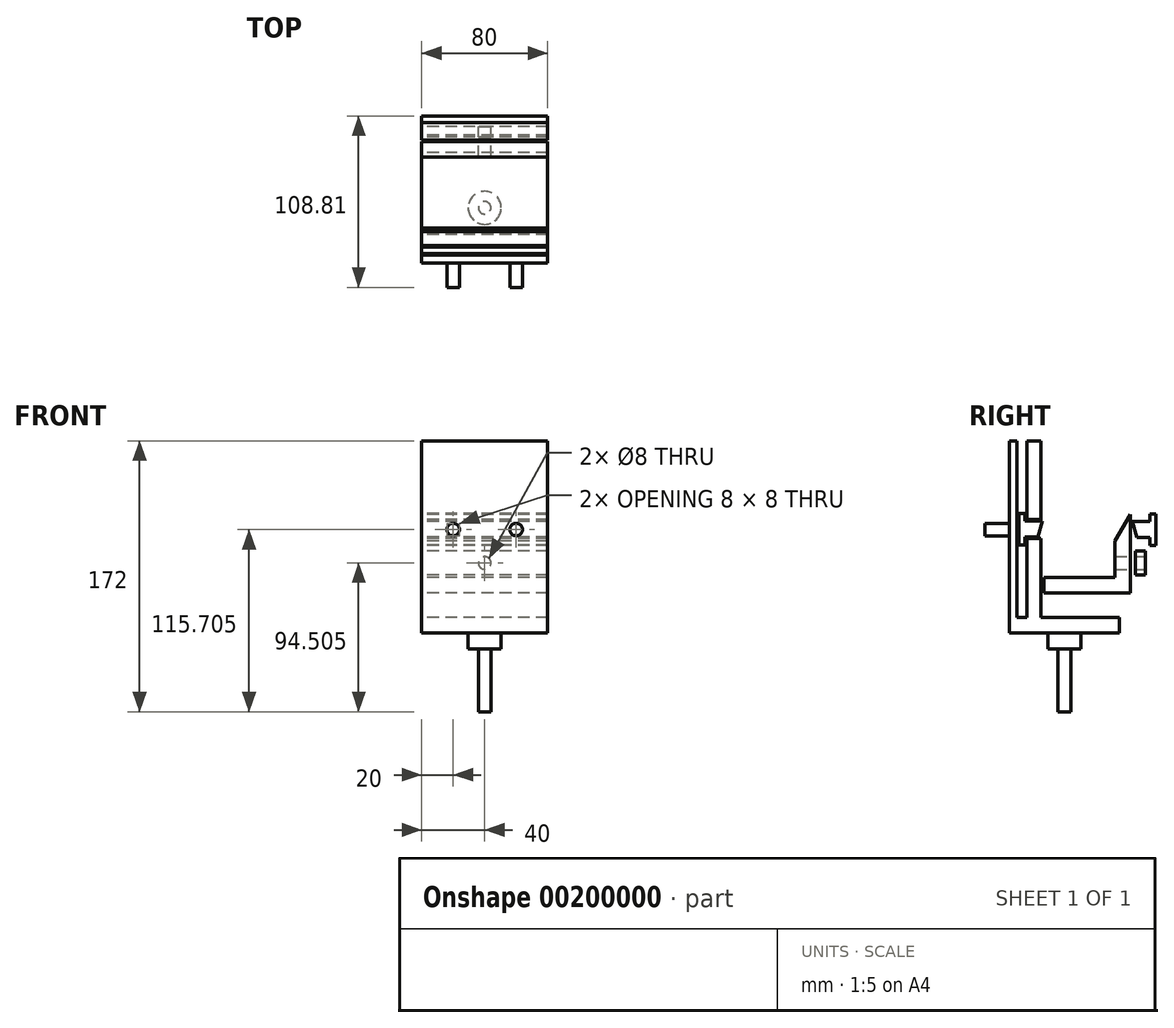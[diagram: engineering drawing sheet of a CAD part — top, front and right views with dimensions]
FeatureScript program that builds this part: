
annotation { "Feature Type Name" : "Feature", "Feature Type Description" : "" }
export const myFeature = defineFeature(function(context is Context, id is Id, definition is map)
    precondition{}
    {
        {
            var Q0;
            Q0=qCreatedBy(makeId("Right.planeOp"),FACE);
            var sketch = newSketch(context, id + "F0", { "sketchPlane" : qUnion([Q0])});
            skLineSegment(sketch, "E0", {"start": v(186.95, -108.62) * mm, "end": v(182.95, -108.62) * mm});
            skLineSegment(sketch, "E1", {"start": v(182.95, -108.62) * mm, "end": v(182.95, -113.62) * mm});
            skLineSegment(sketch, "E2", {"start": v(182.95, -113.62) * mm, "end": v(171.77, -113.62) * mm});
            skLineSegment(sketch, "E3", {"start": v(171.77, -113.62) * mm, "end": v(171.77, -123.62) * mm});
            skLineSegment(sketch, "E4", {"start": v(171.77, -123.62) * mm, "end": v(182.95, -123.62) * mm});
            skLineSegment(sketch, "E5", {"start": v(182.95, -123.62) * mm, "end": v(182.95, -128.62) * mm});
            skLineSegment(sketch, "E6", {"start": v(182.95, -128.62) * mm, "end": v(186.95, -128.62) * mm});
            skLineSegment(sketch, "E7", {"start": v(186.95, -108.62) * mm, "end": v(186.95, -128.62) * mm});
            skLineSegment(sketch, "E8.MirrorCS", {"start": v(103.77, -123.33) * mm, "end": v(103.77, -128.33) * mm});
            skLineSegment(sketch, "E9.MirrorCS", {"start": v(103.77, -108.33) * mm, "end": v(103.77, -113.33) * mm});
            skLineSegment(sketch, "E10.MirrorCS", {"start": v(103.77, -113.33) * mm, "end": v(114.77, -113.33) * mm});
            skLineSegment(sketch, "E11.MirrorCS", {"start": v(114.77, -123.33) * mm, "end": v(103.77, -123.33) * mm});
            skLineSegment(sketch, "E12.MirrorCS", {"start": v(103.77, -128.33) * mm, "end": v(99.77, -128.33) * mm});
            skLineSegment(sketch, "E13.MirrorCS", {"start": v(99.77, -108.33) * mm, "end": v(99.77, -128.33) * mm});
            skLineSegment(sketch, "E14.MirrorCS", {"start": v(99.77, -108.33) * mm, "end": v(103.77, -108.33) * mm});
            skLineSegment(sketch, "E15.MirrorCS", {"start": v(114.77, -113.33) * mm, "end": v(114.77, -123.33) * mm});
            skLineSegment(sketch, "E16.bottom", {"start": v(113.77, -112.33) * mm, "end": v(104.77, -112.33) * mm});
            skLineSegment(sketch, "E16.top", {"start": v(113.77, -62.33) * mm, "end": v(104.77, -62.33) * mm});
            skLineSegment(sketch, "E16.left", {"start": v(113.77, -112.33) * mm, "end": v(113.77, -62.33) * mm});
            skLineSegment(sketch, "E16.right", {"start": v(104.77, -112.33) * mm, "end": v(104.77, -62.33) * mm});
            skLineSegment(sketch, "E17.bottom", {"start": v(113.77, -124.33) * mm, "end": v(104.77, -124.33) * mm});
            skLineSegment(sketch, "E17.top", {"start": v(113.77, -174.33) * mm, "end": v(104.77, -174.33) * mm});
            skLineSegment(sketch, "E17.left", {"start": v(113.77, -124.33) * mm, "end": v(113.77, -174.33) * mm});
            skLineSegment(sketch, "E17.right", {"start": v(104.77, -124.33) * mm, "end": v(104.77, -174.33) * mm});
            skLineSegment(sketch, "E18.bottom", {"start": v(170.77, -109.04) * mm, "end": v(160.77, -109.04) * mm});
            skLineSegment(sketch, "E18.top", {"start": v(170.77, -159.04) * mm, "end": v(160.77, -159.04) * mm});
            skLineSegment(sketch, "E18.left", {"start": v(170.77, -109.04) * mm, "end": v(170.77, -159.04) * mm});
            skLineSegment(sketch, "E18.right", {"start": v(160.77, -109.04) * mm, "end": v(160.77, -159.04) * mm});
            skLineSegment(sketch, "E19.bottom", {"start": v(160.77, -159.04) * mm, "end": v(115.77, -159.04) * mm});
            skLineSegment(sketch, "E19.top", {"start": v(160.77, -149.04) * mm, "end": v(115.77, -149.04) * mm});
            skLineSegment(sketch, "E19.left", {"start": v(160.77, -159.04) * mm, "end": v(160.77, -149.04) * mm});
            skLineSegment(sketch, "E19.right", {"start": v(115.77, -159.04) * mm, "end": v(115.77, -149.04) * mm});
            skLineSegment(sketch, "E20.bottom", {"start": v(115.77, -149.04) * mm, "end": v(125.77, -149.04) * mm});
            skLineSegment(sketch, "E20.top", {"start": v(115.77, -109.04) * mm, "end": v(125.77, -109.04) * mm});
            skLineSegment(sketch, "E20.left", {"start": v(115.77, -149.04) * mm, "end": v(115.77, -109.04) * mm});
            skLineSegment(sketch, "E20.right", {"start": v(125.77, -149.04) * mm, "end": v(125.77, -109.04) * mm});
            skLineSegment(sketch, "E21.bottom", {"start": v(104.77, -174.33) * mm, "end": v(163.76, -174.33) * mm});
            skLineSegment(sketch, "E21.top", {"start": v(104.77, -184.33) * mm, "end": v(163.76, -184.33) * mm});
            skLineSegment(sketch, "E21.left", {"start": v(104.77, -174.33) * mm, "end": v(104.77, -184.33) * mm});
            skLineSegment(sketch, "E21.right", {"start": v(163.76, -174.33) * mm, "end": v(163.76, -184.33) * mm});
            skLineSegment(sketch, "E22.bottom", {"start": v(180.14, -132.3) * mm, "end": v(173.77, -132.3) * mm});
            skLineSegment(sketch, "E22.top", {"start": v(180.14, -147.36) * mm, "end": v(173.77, -147.36) * mm});
            skLineSegment(sketch, "E22.left", {"start": v(180.14, -132.3) * mm, "end": v(180.14, -147.36) * mm});
            skLineSegment(sketch, "E22.right", {"start": v(173.77, -132.3) * mm, "end": v(173.77, -147.36) * mm});
            skLineSegment(sketch, "E23.bottom", {"start": v(98.66, -184.33) * mm, "end": v(93.66, -184.33) * mm});
            skLineSegment(sketch, "E23.top", {"start": v(98.66, -62.33) * mm, "end": v(93.66, -62.33) * mm});
            skLineSegment(sketch, "E23.left", {"start": v(98.66, -184.33) * mm, "end": v(98.66, -62.33) * mm});
            skLineSegment(sketch, "E23.right", {"start": v(93.66, -184.33) * mm, "end": v(93.66, -62.33) * mm});
            skLineSegment(sketch, "E24.bottom", {"start": v(104.77, -174.33) * mm, "end": v(98.66, -174.33) * mm});
            skLineSegment(sketch, "E24.top", {"start": v(104.77, -184.33) * mm, "end": v(98.66, -184.33) * mm});
            skLineSegment(sketch, "E24.right", {"start": v(98.66, -174.33) * mm, "end": v(98.66, -184.33) * mm});
            skLineSegment(sketch, "E25", {"start": v(171.77, -113.62) * mm, "end": v(174.77, -123.62) * mm});
            skLineSegment(sketch, "E26", {"start": v(114.77, -113.33) * mm, "end": v(111.77, -123.33) * mm});
            skLineSegment(sketch, "E27", {"start": v(170.77, -109.04) * mm, "end": v(160.77, -126) * mm});
            skLineSegment(sketch, "E28", {"start": v(115.77, -109.04) * mm, "end": v(125.77, -123.62) * mm});
            skSolve(sketch);
        }
        {
            var Q0;
            Q0=makeQuery(id+"F0.imprint","IMPRINT",FACE,{"disambiguationData":[TD([[makeQuery(id+"F0.imprint","IMPRINT",EDGE,{"derivedFrom":sQuery(id+"F0.wireOp",EDGE,"E19.bottom")}),-1.0]])]});
            var Q1;
            Q1=makeQuery(id+"F0.imprint","IMPRINT",FACE,{"disambiguationData":[TD([[makeQuery(id+"F0.imprint","IMPRINT",EDGE,{"derivedFrom":sQuery(id+"F0.wireOp",EDGE,"E20.bottom")}),1.0]])]});
            var Q2;
            Q2=makeQuery(id+"F0.imprint","IMPRINT",FACE,{"disambiguationData":[TD([[makeQuery(id+"F0.imprint","IMPRINT",EDGE,{"derivedFrom":sQuery(id+"F0.wireOp",EDGE,"E16.bottom")}),-1.0]])]});
            var Q3;
            Q3=makeQuery(id+"F0.imprint","IMPRINT",FACE,{"disambiguationData":[TD([[makeQuery(id+"F0.imprint","IMPRINT",EDGE,{"derivedFrom":sQuery(id+"F0.wireOp",EDGE,"E8.MirrorCS")}),-1.0]])]});
            var Q4;
            Q4=makeQuery(id+"F0.imprint","IMPRINT",FACE,{"disambiguationData":[TD([[makeQuery(id+"F0.imprint","IMPRINT",EDGE,{"derivedFrom":sQuery(id+"F0.wireOp",EDGE,"E17.bottom")}),1.0]])]});
            var Q5;
            Q5=makeQuery(id+"F0.imprint","IMPRINT",FACE,{"disambiguationData":[TD([[makeQuery(id+"F0.imprint","IMPRINT",EDGE,{"derivedFrom":sQuery(id+"F0.wireOp",EDGE,"E0")}),1.0]])]});
            var Q6;
            Q6=makeQuery(id+"F0.imprint","IMPRINT",FACE,{"disambiguationData":[TD([[makeQuery(id+"F0.imprint","IMPRINT",EDGE,{"derivedFrom":sQuery(id+"F0.wireOp",EDGE,"E21.top")}),1.0]])]});
            var Q7;
            Q7=makeQuery(id+"F0.imprint","IMPRINT",FACE,{"disambiguationData":[TD([[makeQuery(id+"F0.imprint","IMPRINT",EDGE,{"derivedFrom":sQuery(id+"F0.wireOp",EDGE,"E22.bottom")}),1.0]])]});
            var Q8;
            Q8=makeQuery(id+"F0.imprint","IMPRINT",FACE,{"disambiguationData":[TD([[makeQuery(id+"F0.imprint","IMPRINT",EDGE,{"derivedFrom":sQuery(id+"F0.wireOp",EDGE,"E23.bottom")}),-1.0]])]});
            var Q9;
            Q9=makeQuery(id+"F0.imprint","IMPRINT",FACE,{"disambiguationData":[TD([[makeQuery(id+"F0.imprint","IMPRINT",EDGE,{"derivedFrom":sQuery(id+"F0.wireOp",EDGE,"E24.bottom")}),1.0]])]});
            var Q10;
            Q10=makeQuery(id+"F0.imprint","IMPRINT",FACE,{"disambiguationData":[TD([[makeQuery(id+"F0.imprint","IMPRINT",EDGE,{"derivedFrom":sQuery(id+"F0.wireOp",EDGE,"E18.top")}),-1.0]])]});
            extrude(context, id + "F1", {"entities" : qUnion([Q0, Q1, Q2, Q3, Q4, Q5, Q6, Q7, Q8, Q9, Q10]), "depth" : 80 * mm});
        }
        {
            var Q0;
            Q0=makeQuery(id+"F1.opExtrude","SWEPT_FACE",FACE,{"disambiguationData":[OSD([sQuery(id+"F0.wireOp",EDGE,"E22.left")])]});
            var sketch = newSketch(context, id + "F2", { "sketchPlane" : qUnion([Q0])});
            skCircle(sketch, "E29", {"center": v(-40, -139.82) * mm, "radius": 4 * mm});
            skPoint(sketch, "E29.centerSnap0", {"position": v(-40, -132.3) * mm});
            skPoint(sketch, "E29.centerSnap1", {"position": v(0, -139.82) * mm});
            skPoint(sketch, "E30", {"position": v(0, -118.62) * mm});
            skCircle(sketch, "E31", {"center": v(-20, -118.62) * mm, "radius": 4 * mm});
            skCircle(sketch, "E32", {"center": v(-60, -118.62) * mm, "radius": 4 * mm});
            skSolve(sketch);
        }
        {
            var Q0;
            Q0=makeQuery(id+"F2.imprint","IMPRINT",FACE,{"disambiguationData":[TD([[makeQuery(id+"F2.imprint","IMPRINT",EDGE,{"derivedFrom":sQuery(id+"F2.wireOp",EDGE,"E31")}),1.0]])]});
            var Q1;
            Q1=makeQuery(id+"F2.imprint","IMPRINT",FACE,{"disambiguationData":[TD([[makeQuery(id+"F2.imprint","IMPRINT",EDGE,{"derivedFrom":sQuery(id+"F2.wireOp",EDGE,"E32")}),1.0]])]});
            var Q2;
            Q2=makeQuery(id+"F1.opExtrude","SWEPT_BODY",BODY,{"disambiguationData":[OSD([sQuery(id+"F0.wireOp",EDGE,"E0"),sQuery(id+"F0.wireOp",EDGE,"E1"),sQuery(id+"F0.wireOp",EDGE,"E2"),sQuery(id+"F0.wireOp",EDGE,"E3"),sQuery(id+"F0.wireOp",EDGE,"E4"),sQuery(id+"F0.wireOp",EDGE,"E5"),sQuery(id+"F0.wireOp",EDGE,"E6"),sQuery(id+"F0.wireOp",EDGE,"E7")])]});
            extrude(context, id + "F3", {"entities" : qUnion([Q0, Q1]), "operationType" : NewBodyOperationType.ADD, "depth" : 1 * mm, "hasSecondDirection" : true, "secondDirectionBound" : SecondDirectionBoundingType.UP_TO_BODY, "secondDirectionOppositeDirection" : true, "secondDirectionBoundEntityBody" : qUnion([Q2]), "secondDirectionDepth" : 25 * mm});
        }
        {
            var Q0;
            Q0=makeQuery(id+"F2.imprint","IMPRINT",FACE,{"disambiguationData":[TD([[makeQuery(id+"F2.imprint","IMPRINT",EDGE,{"derivedFrom":sQuery(id+"F2.wireOp",EDGE,"E29")}),1.0]])]});
            extrude(context, id + "F4", {"entities" : qUnion([Q0]), "operationType" : NewBodyOperationType.REMOVE, "oppositeDirection" : true, "depth" : 36.3 * mm});
        }
        {
            var Q0;
            Q0=makeQuery(id+"F2.imprint","IMPRINT",FACE,{"disambiguationData":[TD([[makeQuery(id+"F2.imprint","IMPRINT",EDGE,{"derivedFrom":sQuery(id+"F2.wireOp",EDGE,"E32")}),1.0]])]});
            var Q1;
            Q1=makeQuery(id+"F2.imprint","IMPRINT",FACE,{"disambiguationData":[TD([[makeQuery(id+"F2.imprint","IMPRINT",EDGE,{"derivedFrom":sQuery(id+"F2.wireOp",EDGE,"E31")}),1.0]])]});
            var Q2;
            Q2=makeQuery(id+"F1.opExtrude","CAP_FACE",FACE,{"disambiguationData":[OSD([sQuery(id+"F0.wireOp",EDGE,"E17.bottom"),sQuery(id+"F0.wireOp",EDGE,"E17.left"),sQuery(id+"F0.wireOp",EDGE,"E17.right"),sQuery(id+"F0.wireOp",EDGE,"E21.bottom"),sQuery(id+"F0.wireOp",EDGE,"E21.top"),sQuery(id+"F0.wireOp",EDGE,"E21.right"),sQuery(id+"F0.wireOp",EDGE,"E23.bottom"),sQuery(id+"F0.wireOp",EDGE,"E23.top"),sQuery(id+"F0.wireOp",EDGE,"E23.left"),sQuery(id+"F0.wireOp",EDGE,"E23.right"),sQuery(id+"F0.wireOp",EDGE,"E24.bottom"),sQuery(id+"F0.wireOp",EDGE,"E24.top")])],"isStart":false});
            extrude(context, id + "F5", {"entities" : qUnion([Q0, Q1]), "operationType" : NewBodyOperationType.REMOVE, "oppositeDirection" : true, "depth" : 200 * mm, "hasSecondDirection" : true, "secondDirectionOppositeDirection" : true, "secondDirectionBoundEntityFace" : qUnion([Q2]), "secondDirectionDepth" : 111 * mm});
        }
        {
            var Q0;
            Q0=makeQuery(id+"F2.imprint","IMPRINT",FACE,{"disambiguationData":[TD([[makeQuery(id+"F2.imprint","IMPRINT",EDGE,{"derivedFrom":sQuery(id+"F2.wireOp",EDGE,"E32")}),1.0]])]});
            var Q1;
            Q1=makeQuery(id+"F2.imprint","IMPRINT",FACE,{"disambiguationData":[TD([[makeQuery(id+"F2.imprint","IMPRINT",EDGE,{"derivedFrom":sQuery(id+"F2.wireOp",EDGE,"E31")}),1.0]])]});
            extrude(context, id + "F6", {"entities" : qUnion([Q0, Q1]), "operationType" : NewBodyOperationType.ADD, "oppositeDirection" : true, "depth" : 102 * mm, "hasSecondDirection" : true, "secondDirectionOppositeDirection" : true, "secondDirectionDepth" : 80 * mm});
        }
        {
            var Q0;
            Q0=makeQuery(id+"F1.opExtrude","SWEPT_FACE",FACE,{"disambiguationData":[OSD([sQuery(id+"F0.wireOp",EDGE,"E21.top"),sQuery(id+"F0.wireOp",EDGE,"E23.bottom"),sQuery(id+"F0.wireOp",EDGE,"E24.top")])]});
            var sketch = newSketch(context, id + "F7", { "sketchPlane" : qUnion([Q0])});
            skCircle(sketch, "E33", {"center": v(40, -128.71) * mm, "radius": 10.5 * mm});
            skPoint(sketch, "E33.centerSnap0", {"position": v(80, -128.71) * mm});
            skPoint(sketch, "E33.centerSnap1", {"position": v(40, -93.66) * mm});
            skCircle(sketch, "E34", {"center": v(40, -128.71) * mm, "radius": 4 * mm});
            skSolve(sketch);
        }
        {
            var Q0;
            Q0=makeQuery(id+"F7.imprint","IMPRINT",FACE,{"disambiguationData":[TD([[makeQuery(id+"F7.imprint","IMPRINT",EDGE,{"derivedFrom":sQuery(id+"F7.wireOp",EDGE,"E34")}),1.0]])]});
            var Q1;
            Q1=sQuery(id+"F7.wireOp",EDGE,"E34");
            extrude(context, id + "F8", {"entities" : qUnion([Q0]), "operationType" : NewBodyOperationType.ADD, "surfaceEntities" : qUnion([Q1]), "depth" : 50 * mm});
        }
        {
            var Q0;
            Q0=makeQuery(id+"F7.imprint","IMPRINT",FACE,{"disambiguationData":[TD([[makeQuery(id+"F7.imprint","IMPRINT",EDGE,{"derivedFrom":sQuery(id+"F7.wireOp",EDGE,"E34")}),1.0]])]});
            var Q1;
            Q1=makeQuery(id+"F7.imprint","IMPRINT",FACE,{"disambiguationData":[TD([[makeQuery(id+"F7.imprint","IMPRINT",EDGE,{"derivedFrom":sQuery(id+"F7.wireOp",EDGE,"E33")}),1.0]])]});
            var Q2;
            Q2=sQuery(id+"F7.wireOp",EDGE,"E33");
            extrude(context, id + "F9", {"entities" : qUnion([Q0, Q1]), "operationType" : NewBodyOperationType.ADD, "surfaceEntities" : qUnion([Q2]), "depth" : 10 * mm});
        }
    });
